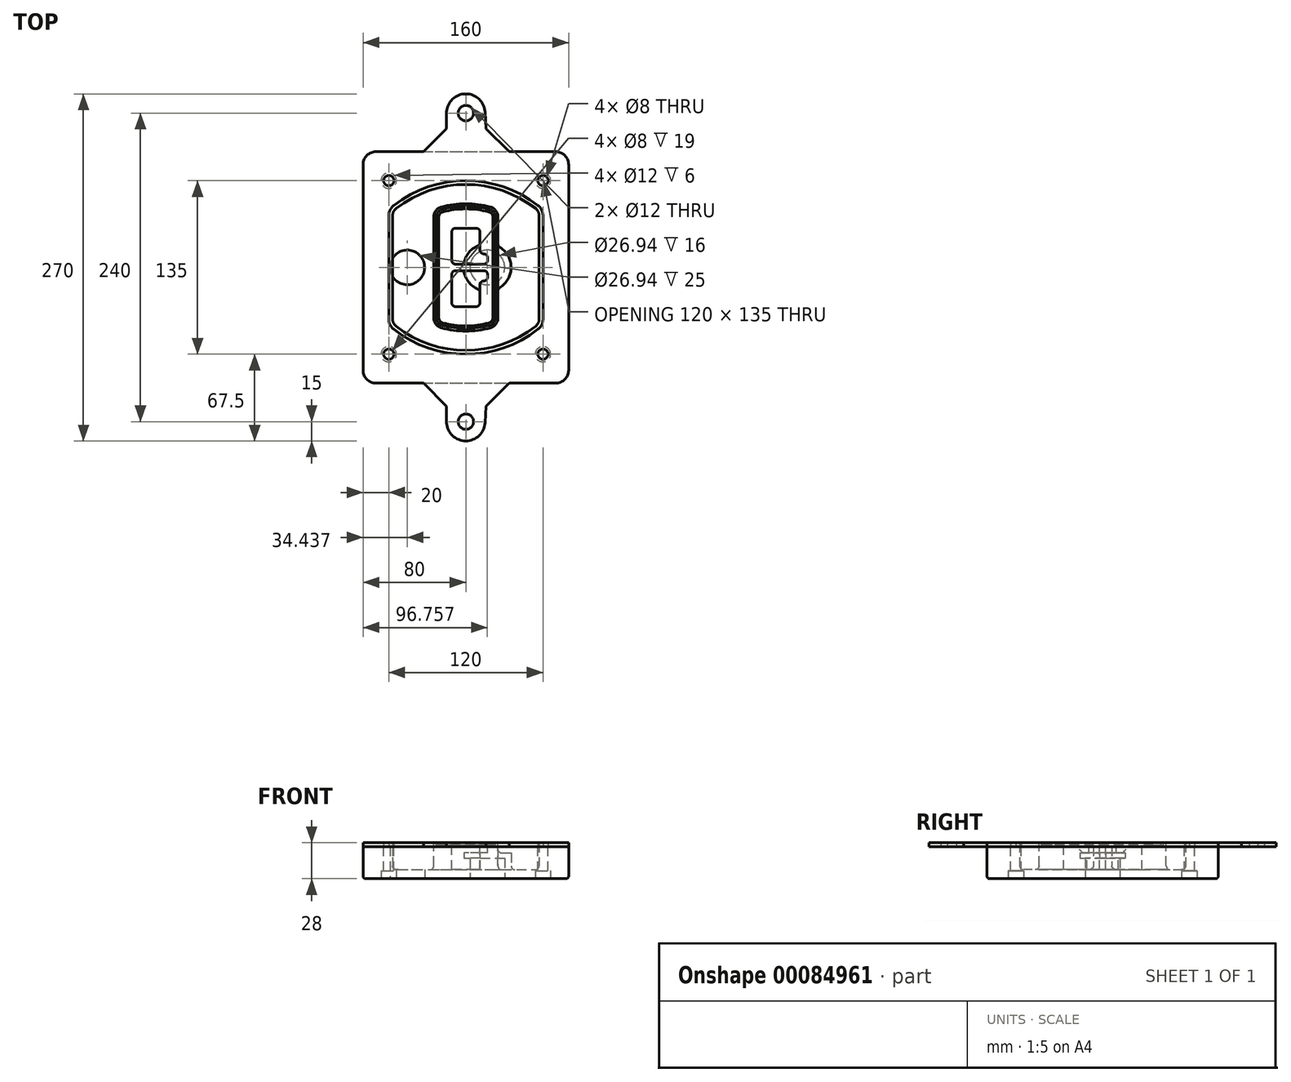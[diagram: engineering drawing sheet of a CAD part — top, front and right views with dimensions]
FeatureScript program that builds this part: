
annotation { "Feature Type Name" : "Feature", "Feature Type Description" : "" }
export const myFeature = defineFeature(function(context is Context, id is Id, definition is map)
    precondition{}
    {
        {
            var Q0;
            Q0=qCreatedBy(makeId("Top.planeOp"),FACE);
            var sketch = newSketch(context, id + "F0", { "sketchPlane" : qUnion([Q0])});
            skPoint(sketch, "E0.rect.middle", {"position": v(0, 0) * mm});
            skLineSegment(sketch, "E1.bottom", {"start": v(-70, -90) * mm, "end": v(70, -90) * mm});
            skLineSegment(sketch, "E1.top", {"start": v(-70, 90) * mm, "end": v(70, 90) * mm});
            skLineSegment(sketch, "E1.left", {"start": v(-80, -80) * mm, "end": v(-80, 80) * mm});
            skLineSegment(sketch, "E1.right", {"start": v(80, -80) * mm, "end": v(80, 80) * mm});
            skLineSegment(sketch, "E2", {"start": v(-80, 90) * mm, "end": v(80, -90) * mm, "construction": true});
            skLineSegment(sketch, "E3", {"start": v(80, 90) * mm, "end": v(-80, -90) * mm, "construction": true});
            skCircle(sketch, "E4", {"center": v(-60, 67.5) * mm, "radius": 4 * mm});
            skCircle(sketch, "E5", {"center": v(60, 67.5) * mm, "radius": 4 * mm});
            skCircle(sketch, "E6", {"center": v(60, -67.5) * mm, "radius": 4 * mm});
            skCircle(sketch, "E7", {"center": v(-60, -67.5) * mm, "radius": 4 * mm});
            skLineSegment(sketch, "E8", {"start": v(-60, 67.5) * mm, "end": v(60, 67.5) * mm, "construction": true});
            skLineSegment(sketch, "E9", {"start": v(60, 67.5) * mm, "end": v(60, -67.5) * mm, "construction": true});
            skLineSegment(sketch, "E10", {"start": v(60, -67.5) * mm, "end": v(-60, -67.5) * mm, "construction": true});
            skLineSegment(sketch, "E11", {"start": v(-60, -67.5) * mm, "end": v(-60, 67.5) * mm, "construction": true});
            skLineSegment(sketch, "E12", {"start": v(-60, 40.3) * mm, "end": v(-60, -40.3) * mm});
            skLineSegment(sketch, "E13", {"start": v(60, 40.3) * mm, "end": v(60, -40.3) * mm});
            skArc(sketch, "E14", {"start": v(56.15, 48.18) * mm, "mid": v(0, 67.5) * mm, "end": v(-56.15, 48.18) * mm});
            skArc(sketch, "E15", {"start": v(-56.15, -48.18) * mm, "mid": v(0, -67.5) * mm, "end": v(56.15, -48.18) * mm});
            skLineSegment(sketch, "E16", {"start": v(-60, 0) * mm, "end": v(60, 0) * mm, "construction": true});
            skPoint(sketch, "E17.visualSharp", {"position": v(-60, -45) * mm});
            skArc(sketch, "E17.filletArc", {"start": v(-60, -40.3) * mm, "mid": v(-58.99, -44.68) * mm, "end": v(-56.15, -48.18) * mm});
            skPoint(sketch, "E18.visualSharp", {"position": v(-60, 45) * mm});
            skArc(sketch, "E18.filletArc", {"start": v(-56.15, 48.18) * mm, "mid": v(-58.99, 44.68) * mm, "end": v(-60, 40.3) * mm});
            skPoint(sketch, "E19.visualSharp", {"position": v(60, 45) * mm});
            skArc(sketch, "E19.filletArc", {"start": v(60, 40.3) * mm, "mid": v(58.99, 44.68) * mm, "end": v(56.15, 48.18) * mm});
            skPoint(sketch, "E20.visualSharp", {"position": v(60, -45) * mm});
            skArc(sketch, "E20.filletArc", {"start": v(56.15, -48.18) * mm, "mid": v(58.99, -44.68) * mm, "end": v(60, -40.3) * mm});
            skPoint(sketch, "E21.visualSharp", {"position": v(-80, 90) * mm});
            skArc(sketch, "E21.filletArc", {"start": v(-70, 90) * mm, "mid": v(-77.07, 87.07) * mm, "end": v(-80, 80) * mm});
            skPoint(sketch, "E22.visualSharp", {"position": v(80, 90) * mm});
            skArc(sketch, "E22.filletArc", {"start": v(80, 80) * mm, "mid": v(77.07, 87.07) * mm, "end": v(70, 90) * mm});
            skPoint(sketch, "E23.visualSharp", {"position": v(80, -90) * mm});
            skArc(sketch, "E23.filletArc", {"start": v(70, -90) * mm, "mid": v(77.07, -87.07) * mm, "end": v(80, -80) * mm});
            skPoint(sketch, "E24.visualSharp", {"position": v(-80, -90) * mm});
            skArc(sketch, "E24.filletArc", {"start": v(-80, -80) * mm, "mid": v(-77.07, -87.07) * mm, "end": v(-70, -90) * mm});
            skArc(sketch, "E25.0", {"start": v(57, 40.3) * mm, "mid": v(56.3, 43.36) * mm, "end": v(54.3, 45.81) * mm});
            skLineSegment(sketch, "E25.1", {"start": v(57, 40.3) * mm, "end": v(57, -40.3) * mm});
            skArc(sketch, "E25.2", {"start": v(54.3, -45.81) * mm, "mid": v(56.3, -43.36) * mm, "end": v(57, -40.3) * mm});
            skArc(sketch, "E25.3", {"start": v(-54.3, -45.81) * mm, "mid": v(0, -64.5) * mm, "end": v(54.3, -45.81) * mm});
            skArc(sketch, "E25.4", {"start": v(-57, -40.3) * mm, "mid": v(-56.3, -43.36) * mm, "end": v(-54.3, -45.81) * mm});
            skArc(sketch, "E25.5", {"start": v(54.3, 45.81) * mm, "mid": v(0, 64.5) * mm, "end": v(-54.3, 45.81) * mm});
            skLineSegment(sketch, "E25.6", {"start": v(-57, 40.3) * mm, "end": v(-57, -40.3) * mm});
            skArc(sketch, "E25.7", {"start": v(-54.3, 45.81) * mm, "mid": v(-56.3, 43.36) * mm, "end": v(-57, 40.3) * mm});
            skArc(sketch, "E26.0", {"start": v(-58.62, 51.33) * mm, "mid": v(-62.58, 46.43) * mm, "end": v(-64, 40.3) * mm});
            skArc(sketch, "E26.1", {"start": v(58.62, 51.33) * mm, "mid": v(0, 71.5) * mm, "end": v(-58.62, 51.33) * mm});
            skArc(sketch, "E26.2", {"start": v(64, 40.3) * mm, "mid": v(62.58, 46.43) * mm, "end": v(58.62, 51.33) * mm});
            skLineSegment(sketch, "E26.3", {"start": v(64, 40.3) * mm, "end": v(64, -40.3) * mm});
            skArc(sketch, "E26.4", {"start": v(58.62, -51.33) * mm, "mid": v(62.58, -46.43) * mm, "end": v(64, -40.3) * mm});
            skLineSegment(sketch, "E26.5", {"start": v(-64, 40.3) * mm, "end": v(-64, -40.3) * mm});
            skArc(sketch, "E26.6", {"start": v(-58.62, -51.33) * mm, "mid": v(0, -71.5) * mm, "end": v(58.62, -51.33) * mm});
            skArc(sketch, "E26.7", {"start": v(-64, -40.3) * mm, "mid": v(-62.58, -46.43) * mm, "end": v(-58.62, -51.33) * mm});
            skSolve(sketch);
        }
        {
            var Q0;
            Q0=makeQuery(id+"F0.imprint","IMPRINT",FACE,{"disambiguationData":[TD([[makeQuery(id+"F0.imprint","IMPRINT",EDGE,{"derivedFrom":sQuery(id+"F0.wireOp",EDGE,"E1.bottom")}),1.0]])]});
            var Q1;
            Q1=makeQuery(id+"F0.imprint","IMPRINT",FACE,{"disambiguationData":[TD([[makeQuery(id+"F0.imprint","IMPRINT",EDGE,{"derivedFrom":sQuery(id+"F0.wireOp",EDGE,"E12")}),1.0]])]});
            var Q2;
            Q2=makeQuery(id+"F0.imprint","IMPRINT",FACE,{"disambiguationData":[TD([[makeQuery(id+"F0.imprint","IMPRINT",EDGE,{"derivedFrom":sQuery(id+"F0.wireOp",EDGE,"E25.0")}),1.0]])]});
            var Q3;
            Q3=makeQuery(id+"F0.imprint","IMPRINT",FACE,{"disambiguationData":[TD([[makeQuery(id+"F0.imprint","IMPRINT",EDGE,{"derivedFrom":sQuery(id+"F0.wireOp",EDGE,"E12")}),-1.0]])]});
            extrude(context, id + "F1", {"entities" : qUnion([Q0, Q1, Q2, Q3]), "oppositeDirection" : true, "depth" : 25 * mm});
        }
        {
            var Q0;
            Q0=makeQuery(id+"F0.imprint","IMPRINT",FACE,{"disambiguationData":[TD([[makeQuery(id+"F0.imprint","IMPRINT",EDGE,{"derivedFrom":sQuery(id+"F0.wireOp",EDGE,"E12")}),1.0]])]});
            extrude(context, id + "F2", {"entities" : qUnion([Q0]), "operationType" : NewBodyOperationType.ADD, "depth" : 3 * mm});
        }
        {
            var Q0;
            Q0=makeQuery(id+"F0.imprint","IMPRINT",FACE,{"disambiguationData":[TD([[makeQuery(id+"F0.imprint","IMPRINT",EDGE,{"derivedFrom":sQuery(id+"F0.wireOp",EDGE,"E25.0")}),1.0]])]});
            extrude(context, id + "F3", {"entities" : qUnion([Q0]), "operationType" : NewBodyOperationType.REMOVE, "oppositeDirection" : true, "depth" : 18 * mm});
        }
        {
            var Q0;
            Q0=makeQuery(id+"F2.opExtrude","CAP_FACE",FACE,{"disambiguationData":[OSD([sQuery(id+"F0.wireOp",EDGE,"E12"),sQuery(id+"F0.wireOp",EDGE,"E13"),sQuery(id+"F0.wireOp",EDGE,"E14"),sQuery(id+"F0.wireOp",EDGE,"E15"),sQuery(id+"F0.wireOp",EDGE,"E17.filletArc"),sQuery(id+"F0.wireOp",EDGE,"E18.filletArc"),sQuery(id+"F0.wireOp",EDGE,"E19.filletArc"),sQuery(id+"F0.wireOp",EDGE,"E20.filletArc"),sQuery(id+"F0.wireOp",EDGE,"E25.0"),sQuery(id+"F0.wireOp",EDGE,"E25.1"),sQuery(id+"F0.wireOp",EDGE,"E25.2"),sQuery(id+"F0.wireOp",EDGE,"E25.3"),sQuery(id+"F0.wireOp",EDGE,"E25.4"),sQuery(id+"F0.wireOp",EDGE,"E25.5"),sQuery(id+"F0.wireOp",EDGE,"E25.6"),sQuery(id+"F0.wireOp",EDGE,"E25.7")])],"isStart":false});
            var sketch = newSketch(context, id + "F4", { "sketchPlane" : qUnion([Q0])});
            skArc(sketch, "E27.0", {"start": v(-19.08, -46.97) * mm, "mid": v(0, -49.5) * mm, "end": v(19.08, -46.97) * mm});
            skArc(sketch, "E28.0", {"start": v(19.08, 46.97) * mm, "mid": v(0, 49.5) * mm, "end": v(-19.08, 46.97) * mm});
            skLineSegment(sketch, "E29", {"start": v(-25, 39.25) * mm, "end": v(-25, -39.25) * mm});
            skLineSegment(sketch, "E30", {"start": v(25, 39.25) * mm, "end": v(25, -39.25) * mm});
            skLineSegment(sketch, "E31", {"start": v(-25, 45.1) * mm, "end": v(25, 45.1) * mm, "construction": true});
            skLineSegment(sketch, "E32", {"start": v(-25, -45.1) * mm, "end": v(25, -45.1) * mm, "construction": true});
            skPoint(sketch, "E33.visualSharp", {"position": v(-25, 45.1) * mm});
            skArc(sketch, "E33.filletArc", {"start": v(-19.08, 46.97) * mm, "mid": v(-23.35, 44.11) * mm, "end": v(-25, 39.25) * mm});
            skPoint(sketch, "E34.visualSharp", {"position": v(25, 45.1) * mm});
            skArc(sketch, "E34.filletArc", {"start": v(25, 39.25) * mm, "mid": v(23.35, 44.11) * mm, "end": v(19.08, 46.97) * mm});
            skPoint(sketch, "E35.visualSharp", {"position": v(25, -45.1) * mm});
            skArc(sketch, "E35.filletArc", {"start": v(19.08, -46.97) * mm, "mid": v(23.35, -44.11) * mm, "end": v(25, -39.25) * mm});
            skPoint(sketch, "E36.visualSharp", {"position": v(-25, -45.1) * mm});
            skArc(sketch, "E36.filletArc", {"start": v(-25, -39.25) * mm, "mid": v(-23.35, -44.11) * mm, "end": v(-19.08, -46.97) * mm});
            skArc(sketch, "E37.0", {"start": v(54.3, 45.81) * mm, "mid": v(0, 64.5) * mm, "end": v(-54.3, 45.81) * mm});
            skArc(sketch, "E37.1", {"start": v(-54.3, 45.81) * mm, "mid": v(-56.3, 43.36) * mm, "end": v(-57, 40.3) * mm});
            skLineSegment(sketch, "E37.2", {"start": v(-57, 40.3) * mm, "end": v(-57, -40.3) * mm});
            skArc(sketch, "E37.3", {"start": v(-57, -40.3) * mm, "mid": v(-56.3, -43.36) * mm, "end": v(-54.3, -45.81) * mm});
            skArc(sketch, "E37.4", {"start": v(-54.3, -45.81) * mm, "mid": v(0, -64.5) * mm, "end": v(54.3, -45.81) * mm});
            skArc(sketch, "E37.5", {"start": v(54.3, -45.81) * mm, "mid": v(56.3, -43.36) * mm, "end": v(57, -40.3) * mm});
            skLineSegment(sketch, "E37.6", {"start": v(57, 40.3) * mm, "end": v(57, -40.3) * mm});
            skArc(sketch, "E37.7", {"start": v(57, 40.3) * mm, "mid": v(56.3, 43.36) * mm, "end": v(54.3, 45.81) * mm});
            skLineSegment(sketch, "E38.0", {"start": v(23, 39.25) * mm, "end": v(23, -39.25) * mm});
            skArc(sketch, "E38.1", {"start": v(18.56, -45.04) * mm, "mid": v(21.76, -42.9) * mm, "end": v(23, -39.25) * mm});
            skArc(sketch, "E38.2", {"start": v(-18.56, -45.04) * mm, "mid": v(0, -47.5) * mm, "end": v(18.56, -45.04) * mm});
            skArc(sketch, "E38.3", {"start": v(-23, -39.25) * mm, "mid": v(-21.76, -42.9) * mm, "end": v(-18.56, -45.04) * mm});
            skLineSegment(sketch, "E38.4", {"start": v(-23, 39.25) * mm, "end": v(-23, -39.25) * mm});
            skArc(sketch, "E38.5", {"start": v(23, 39.25) * mm, "mid": v(21.76, 42.9) * mm, "end": v(18.56, 45.04) * mm});
            skArc(sketch, "E38.6", {"start": v(-18.56, 45.04) * mm, "mid": v(-21.76, 42.9) * mm, "end": v(-23, 39.25) * mm});
            skArc(sketch, "E38.7", {"start": v(18.56, 45.04) * mm, "mid": v(0, 47.5) * mm, "end": v(-18.56, 45.04) * mm});
            skArc(sketch, "E39.0", {"start": v(21, 39.25) * mm, "mid": v(20.18, 41.68) * mm, "end": v(18.04, 43.1) * mm});
            skLineSegment(sketch, "E39.1", {"start": v(21, 39.25) * mm, "end": v(21, -39.25) * mm});
            skArc(sketch, "E39.2", {"start": v(18.04, -43.1) * mm, "mid": v(20.18, -41.68) * mm, "end": v(21, -39.25) * mm});
            skArc(sketch, "E39.3", {"start": v(-18.04, -43.1) * mm, "mid": v(0, -45.5) * mm, "end": v(18.04, -43.1) * mm});
            skArc(sketch, "E39.4", {"start": v(-21, -39.25) * mm, "mid": v(-20.18, -41.68) * mm, "end": v(-18.04, -43.1) * mm});
            skArc(sketch, "E39.5", {"start": v(18.04, 43.1) * mm, "mid": v(0, 45.5) * mm, "end": v(-18.04, 43.1) * mm});
            skLineSegment(sketch, "E39.6", {"start": v(-21, 39.25) * mm, "end": v(-21, -39.25) * mm});
            skArc(sketch, "E39.7", {"start": v(-18.04, 43.1) * mm, "mid": v(-20.18, 41.68) * mm, "end": v(-21, 39.25) * mm});
            skLineSegment(sketch, "E40", {"start": v(-25, 0) * mm, "end": v(25, 0) * mm, "construction": true});
            skLineSegment(sketch, "E41", {"start": v(-11, 5.5) * mm, "end": v(-11, 27.5) * mm});
            skLineSegment(sketch, "E42", {"start": v(-8, 30.5) * mm, "end": v(8, 30.5) * mm});
            skLineSegment(sketch, "E43", {"start": v(11, 27.5) * mm, "end": v(11, 13.5) * mm});
            skLineSegment(sketch, "E44", {"start": v(14, 10.5) * mm, "end": v(14, 10.5) * mm});
            skLineSegment(sketch, "E45", {"start": v(17, 7.5) * mm, "end": v(17, 5.5) * mm});
            skLineSegment(sketch, "E46", {"start": v(14, 2.5) * mm, "end": v(-8, 2.5) * mm});
            skPoint(sketch, "E47.visualSharp", {"position": v(-11, 30.5) * mm});
            skArc(sketch, "E47.filletArc", {"start": v(-8, 30.5) * mm, "mid": v(-10.12, 29.62) * mm, "end": v(-11, 27.5) * mm});
            skPoint(sketch, "E48.visualSharp", {"position": v(11, 30.5) * mm});
            skArc(sketch, "E48.filletArc", {"start": v(11, 27.5) * mm, "mid": v(10.12, 29.62) * mm, "end": v(8, 30.5) * mm});
            skPoint(sketch, "E49.visualSharp", {"position": v(11, 10.5) * mm});
            skArc(sketch, "E49.filletArc", {"start": v(11, 13.5) * mm, "mid": v(11.88, 11.38) * mm, "end": v(14, 10.5) * mm});
            skPoint(sketch, "E50.visualSharp", {"position": v(17, 10.5) * mm});
            skArc(sketch, "E50.filletArc", {"start": v(17, 7.5) * mm, "mid": v(16.12, 9.62) * mm, "end": v(14, 10.5) * mm});
            skPoint(sketch, "E51.visualSharp", {"position": v(17, 2.5) * mm});
            skArc(sketch, "E51.filletArc", {"start": v(14, 2.5) * mm, "mid": v(16.12, 3.38) * mm, "end": v(17, 5.5) * mm});
            skPoint(sketch, "E52.visualSharp", {"position": v(-11, 2.5) * mm});
            skArc(sketch, "E52.filletArc", {"start": v(-11, 5.5) * mm, "mid": v(-10.12, 3.38) * mm, "end": v(-8, 2.5) * mm});
            skLineSegment(sketch, "E53.0.MirrorCS", {"start": v(14, -2.5) * mm, "end": v(-8, -2.5) * mm});
            skArc(sketch, "E54.0.MirrorCS", {"start": v(-11, -5.5) * mm, "mid": v(-10.12, -3.38) * mm, "end": v(-8, -2.5) * mm});
            skLineSegment(sketch, "E55.0.MirrorCS", {"start": v(-11, -5.5) * mm, "end": v(-11, -27.5) * mm});
            skArc(sketch, "E56.0.MirrorCS", {"start": v(-8, -30.5) * mm, "mid": v(-10.12, -29.62) * mm, "end": v(-11, -27.5) * mm});
            skLineSegment(sketch, "E57.0.MirrorCS", {"start": v(-8, -30.5) * mm, "end": v(8, -30.5) * mm});
            skArc(sketch, "E58.0.MirrorCS", {"start": v(11, -27.5) * mm, "mid": v(10.12, -29.62) * mm, "end": v(8, -30.5) * mm});
            skLineSegment(sketch, "E59.0.MirrorCS", {"start": v(11, -27.5) * mm, "end": v(11, -13.5) * mm});
            skArc(sketch, "E60.0.MirrorCS", {"start": v(11, -13.5) * mm, "mid": v(11.88, -11.38) * mm, "end": v(14, -10.5) * mm});
            skArc(sketch, "E61.0.MirrorCS", {"start": v(17, -7.5) * mm, "mid": v(16.12, -9.62) * mm, "end": v(14, -10.5) * mm});
            skLineSegment(sketch, "E62.0.MirrorCS", {"start": v(17, -7.5) * mm, "end": v(17, -5.5) * mm});
            skArc(sketch, "E63.0.MirrorCS", {"start": v(14, -2.5) * mm, "mid": v(16.12, -3.38) * mm, "end": v(17, -5.5) * mm});
            skSolve(sketch);
        }
        {
            var Q0;
            Q0=makeQuery(id+"F4.imprint","IMPRINT",FACE,{"disambiguationData":[TD([[makeQuery(id+"F4.imprint","IMPRINT",EDGE,{"derivedFrom":sQuery(id+"F4.wireOp",EDGE,"E27.0")}),1.0]])]});
            var Q1;
            Q1=makeQuery(id+"F4.imprint","IMPRINT",FACE,{"disambiguationData":[TD([[makeQuery(id+"F4.imprint","IMPRINT",EDGE,{"derivedFrom":sQuery(id+"F4.wireOp",EDGE,"E38.0")}),-1.0]])]});
            var Q2;
            Q2=makeQuery(id+"F4.imprint","IMPRINT",FACE,{"disambiguationData":[TD([[makeQuery(id+"F4.imprint","IMPRINT",EDGE,{"derivedFrom":sQuery(id+"F4.wireOp",EDGE,"E39.0")}),1.0]])]});
            extrude(context, id + "F5", {"entities" : qUnion([Q0, Q1, Q2]), "operationType" : NewBodyOperationType.ADD, "endBound" : BoundingType.UP_TO_NEXT, "oppositeDirection" : true, "depth" : 25 * mm});
        }
        {
            var Q0;
            Q0=makeQuery(id+"F4.imprint","IMPRINT",FACE,{"disambiguationData":[TD([[makeQuery(id+"F4.imprint","IMPRINT",EDGE,{"derivedFrom":sQuery(id+"F4.wireOp",EDGE,"E38.0")}),-1.0]])]});
            extrude(context, id + "F6", {"entities" : qUnion([Q0]), "operationType" : NewBodyOperationType.REMOVE, "oppositeDirection" : true, "depth" : 2 * mm});
        }
        {
            var Q0;
            Q0=makeQuery(id+"F1.opExtrude","CAP_FACE",FACE,{"disambiguationData":[OSD([sQuery(id+"F0.wireOp",EDGE,"E1.bottom"),sQuery(id+"F0.wireOp",EDGE,"E1.top"),sQuery(id+"F0.wireOp",EDGE,"E1.left"),sQuery(id+"F0.wireOp",EDGE,"E1.right"),sQuery(id+"F0.wireOp",EDGE,"E4"),sQuery(id+"F0.wireOp",EDGE,"E5"),sQuery(id+"F0.wireOp",EDGE,"E6"),sQuery(id+"F0.wireOp",EDGE,"E7"),sQuery(id+"F0.wireOp",EDGE,"E21.filletArc"),sQuery(id+"F0.wireOp",EDGE,"E22.filletArc"),sQuery(id+"F0.wireOp",EDGE,"E23.filletArc"),sQuery(id+"F0.wireOp",EDGE,"E24.filletArc")])],"isStart":false});
            var sketch = newSketch(context, id + "F7", { "sketchPlane" : qUnion([Q0])});
            skCircle(sketch, "E64", {"center": v(16.76, 0) * mm, "radius": 13.47 * mm});
            skCircle(sketch, "E65", {"center": v(-45.56, 0) * mm, "radius": 13.47 * mm});
            skLineSegment(sketch, "E66", {"start": v(80, 0) * mm, "end": v(-80, 0) * mm});
            skCircle(sketch, "E67", {"center": v(16.76, 0) * mm, "radius": 18.47 * mm});
            skCircle(sketch, "E68", {"center": v(60, -67.5) * mm, "radius": 6 * mm});
            skCircle(sketch, "E69", {"center": v(-60, -67.5) * mm, "radius": 6 * mm});
            skCircle(sketch, "E70", {"center": v(-60, 67.5) * mm, "radius": 6 * mm});
            skCircle(sketch, "E71", {"center": v(60, 67.5) * mm, "radius": 6 * mm});
            skSolve(sketch);
        }
        {
            var Q0;
            {var subQ1=sQuery(id+"F7.wireOp",EDGE,"E66");var subQ4=sQuery(id+"F7.wireOp",EDGE,"E64");var subQ6=makeQuery(id+"F7.imprint","INTERSECT",VERTEX,{"disambiguationData":[OD(0.0)],"derivedFrom":[subQ4,subQ1]});Q0=makeQuery(id+"F7.imprint","IMPRINT",FACE,{"disambiguationData":[TD([[makeQuery(id+"F7.imprint","IMPRINT",EDGE,{"disambiguationData":[TD([[subQ6,-1.0]])],"derivedFrom":subQ4}),-1.0]])]});}
            var Q1;
            {var subQ0=sQuery(id+"F7.wireOp",EDGE,"E66");var subQ1=sQuery(id+"F7.wireOp",EDGE,"E64");var subQ3=makeQuery(id+"F7.imprint","INTERSECT",VERTEX,{"disambiguationData":[OD(0.0)],"derivedFrom":[subQ1,subQ0]});Q1=makeQuery(id+"F7.imprint","IMPRINT",FACE,{"disambiguationData":[TD([[makeQuery(id+"F7.imprint","IMPRINT",EDGE,{"disambiguationData":[TD([[subQ3,-1.0]])],"derivedFrom":subQ1}),1.0]])]});}
            var Q2;
            {var subQ0=sQuery(id+"F7.wireOp",EDGE,"E66");var subQ1=sQuery(id+"F7.wireOp",EDGE,"E64");var subQ3=makeQuery(id+"F7.imprint","INTERSECT",VERTEX,{"disambiguationData":[OD(0.0)],"derivedFrom":[subQ1,subQ0]});Q2=makeQuery(id+"F7.imprint","IMPRINT",FACE,{"disambiguationData":[TD([[makeQuery(id+"F7.imprint","IMPRINT",EDGE,{"disambiguationData":[TD([[subQ3,1.0]])],"derivedFrom":subQ1}),1.0]])]});}
            var Q3;
            {var subQ1=sQuery(id+"F7.wireOp",EDGE,"E66");var subQ4=sQuery(id+"F7.wireOp",EDGE,"E64");var subQ6=makeQuery(id+"F7.imprint","INTERSECT",VERTEX,{"disambiguationData":[OD(0.0)],"derivedFrom":[subQ4,subQ1]});Q3=makeQuery(id+"F7.imprint","IMPRINT",FACE,{"disambiguationData":[TD([[makeQuery(id+"F7.imprint","IMPRINT",EDGE,{"disambiguationData":[TD([[subQ6,1.0]])],"derivedFrom":subQ4}),-1.0]])]});}
            extrude(context, id + "F8", {"entities" : qUnion([Q0, Q1, Q2, Q3]), "operationType" : NewBodyOperationType.ADD, "oppositeDirection" : true, "depth" : 20 * mm});
        }
        {
            var Q0;
            {var subQ0=sQuery(id+"F7.wireOp",EDGE,"E66");var subQ1=sQuery(id+"F7.wireOp",EDGE,"E64");var subQ3=makeQuery(id+"F7.imprint","INTERSECT",VERTEX,{"disambiguationData":[OD(0.0)],"derivedFrom":[subQ1,subQ0]});Q0=makeQuery(id+"F7.imprint","IMPRINT",FACE,{"disambiguationData":[TD([[makeQuery(id+"F7.imprint","IMPRINT",EDGE,{"disambiguationData":[TD([[subQ3,-1.0]])],"derivedFrom":subQ1}),1.0]])]});}
            var Q1;
            {var subQ0=sQuery(id+"F7.wireOp",EDGE,"E66");var subQ1=sQuery(id+"F7.wireOp",EDGE,"E64");var subQ3=makeQuery(id+"F7.imprint","INTERSECT",VERTEX,{"disambiguationData":[OD(0.0)],"derivedFrom":[subQ1,subQ0]});Q1=makeQuery(id+"F7.imprint","IMPRINT",FACE,{"disambiguationData":[TD([[makeQuery(id+"F7.imprint","IMPRINT",EDGE,{"disambiguationData":[TD([[subQ3,1.0]])],"derivedFrom":subQ1}),1.0]])]});}
            extrude(context, id + "F9", {"entities" : qUnion([Q0, Q1]), "operationType" : NewBodyOperationType.REMOVE, "oppositeDirection" : true, "depth" : 16 * mm});
        }
        {
            var Q0;
            {var subQ0=sQuery(id+"F7.wireOp",EDGE,"E66");var subQ1=sQuery(id+"F7.wireOp",EDGE,"E65");var subQ3=makeQuery(id+"F7.imprint","INTERSECT",VERTEX,{"disambiguationData":[OD(0.0)],"derivedFrom":[subQ1,subQ0]});Q0=makeQuery(id+"F7.imprint","IMPRINT",FACE,{"disambiguationData":[TD([[makeQuery(id+"F7.imprint","IMPRINT",EDGE,{"disambiguationData":[TD([[subQ3,-1.0]])],"derivedFrom":subQ1}),1.0]])]});}
            var Q1;
            {var subQ0=sQuery(id+"F7.wireOp",EDGE,"E66");var subQ1=sQuery(id+"F7.wireOp",EDGE,"E65");var subQ3=makeQuery(id+"F7.imprint","INTERSECT",VERTEX,{"disambiguationData":[OD(0.0)],"derivedFrom":[subQ1,subQ0]});Q1=makeQuery(id+"F7.imprint","IMPRINT",FACE,{"disambiguationData":[TD([[makeQuery(id+"F7.imprint","IMPRINT",EDGE,{"disambiguationData":[TD([[subQ3,1.0]])],"derivedFrom":subQ1}),1.0]])]});}
            extrude(context, id + "F10", {"entities" : qUnion([Q0, Q1]), "operationType" : NewBodyOperationType.REMOVE, "oppositeDirection" : true, "depth" : 25 * mm});
        }
        {
            var Q0;
            Q0=makeQuery(id+"F7.imprint","IMPRINT",FACE,{"disambiguationData":[TD([[makeQuery(id+"F7.imprint","IMPRINT",EDGE,{"derivedFrom":sQuery(id+"F7.wireOp",EDGE,"E68")}),1.0]])]});
            var Q1;
            Q1=makeQuery(id+"F7.imprint","IMPRINT",FACE,{"disambiguationData":[TD([[makeQuery(id+"F7.imprint","IMPRINT",EDGE,{"derivedFrom":makeQuery(id+"F1.opExtrude","CAP_EDGE",EDGE,{"disambiguationData":[OSD([sQuery(id+"F0.wireOp",EDGE,"E5")])],"isStart":false})}),-1.0]])]});
            var Q2;
            Q2=makeQuery(id+"F7.imprint","IMPRINT",FACE,{"disambiguationData":[TD([[makeQuery(id+"F7.imprint","IMPRINT",EDGE,{"derivedFrom":sQuery(id+"F7.wireOp",EDGE,"E69")}),1.0]])]});
            var Q3;
            Q3=makeQuery(id+"F7.imprint","IMPRINT",FACE,{"disambiguationData":[TD([[makeQuery(id+"F7.imprint","IMPRINT",EDGE,{"derivedFrom":makeQuery(id+"F1.opExtrude","CAP_EDGE",EDGE,{"disambiguationData":[OSD([sQuery(id+"F0.wireOp",EDGE,"E4")])],"isStart":false})}),-1.0]])]});
            var Q4;
            Q4=makeQuery(id+"F7.imprint","IMPRINT",FACE,{"disambiguationData":[TD([[makeQuery(id+"F7.imprint","IMPRINT",EDGE,{"derivedFrom":sQuery(id+"F7.wireOp",EDGE,"E70")}),1.0]])]});
            var Q5;
            Q5=makeQuery(id+"F7.imprint","IMPRINT",FACE,{"disambiguationData":[TD([[makeQuery(id+"F7.imprint","IMPRINT",EDGE,{"derivedFrom":makeQuery(id+"F1.opExtrude","CAP_EDGE",EDGE,{"disambiguationData":[OSD([sQuery(id+"F0.wireOp",EDGE,"E7")])],"isStart":false})}),-1.0]])]});
            var Q6;
            Q6=makeQuery(id+"F7.imprint","IMPRINT",FACE,{"disambiguationData":[TD([[makeQuery(id+"F7.imprint","IMPRINT",EDGE,{"derivedFrom":sQuery(id+"F7.wireOp",EDGE,"E71")}),1.0]])]});
            var Q7;
            Q7=makeQuery(id+"F7.imprint","IMPRINT",FACE,{"disambiguationData":[TD([[makeQuery(id+"F7.imprint","IMPRINT",EDGE,{"derivedFrom":makeQuery(id+"F1.opExtrude","CAP_EDGE",EDGE,{"disambiguationData":[OSD([sQuery(id+"F0.wireOp",EDGE,"E6")])],"isStart":false})}),-1.0]])]});
            extrude(context, id + "F11", {"entities" : qUnion([Q0, Q1, Q2, Q3, Q4, Q5, Q6, Q7]), "operationType" : NewBodyOperationType.REMOVE, "oppositeDirection" : true, "depth" : 6 * mm});
        }
        {
            var Q0;
            Q0=makeQuery(id+"F9.boolean.opBoolean","COPY",FACE,{"derivedFrom":makeQuery(id+"F9.opExtrude","CAP_FACE",FACE,{"disambiguationData":[OSD([sQuery(id+"F7.wireOp",EDGE,"E64")])],"isStart":false})});
            var sketch = newSketch(context, id + "F12", { "sketchPlane" : qUnion([Q0])});
            skArc(sketch, "E72.0", {"start": v(11, 17.55) * mm, "mid": v(2.57, 11.82) * mm, "end": v(-1.54, 2.5) * mm});
            skArc(sketch, "E72.1", {"start": v(-1.54, -2.5) * mm, "mid": v(2.57, -11.82) * mm, "end": v(11, -17.55) * mm});
            skLineSegment(sketch, "E73", {"start": v(-1.54, -2.5) * mm, "end": v(14, -2.5) * mm});
            skLineSegment(sketch, "E74.0", {"start": v(14, 2.5) * mm, "end": v(-1.54, 2.5) * mm});
            skArc(sketch, "E74.1", {"start": v(14, 2.5) * mm, "mid": v(16.12, 3.38) * mm, "end": v(17, 5.5) * mm});
            skLineSegment(sketch, "E74.2", {"start": v(17, 7.5) * mm, "end": v(17, 5.5) * mm});
            skArc(sketch, "E74.3", {"start": v(17, 7.5) * mm, "mid": v(16.12, 9.62) * mm, "end": v(14, 10.5) * mm});
            skArc(sketch, "E74.4", {"start": v(11, 13.5) * mm, "mid": v(11.88, 11.38) * mm, "end": v(14, 10.5) * mm});
            skLineSegment(sketch, "E74.5", {"start": v(11, 17.55) * mm, "end": v(11, 13.5) * mm});
            skLineSegment(sketch, "E74.7", {"start": v(14, -2.5) * mm, "end": v(-1.54, -2.5) * mm});
            skArc(sketch, "E74.8", {"start": v(14, -2.5) * mm, "mid": v(16.12, -3.38) * mm, "end": v(17, -5.5) * mm});
            skLineSegment(sketch, "E74.9", {"start": v(17, -7.5) * mm, "end": v(17, -5.5) * mm});
            skArc(sketch, "E74.10", {"start": v(17, -7.5) * mm, "mid": v(16.12, -9.62) * mm, "end": v(14, -10.5) * mm});
            skArc(sketch, "E74.11", {"start": v(11, -13.5) * mm, "mid": v(11.88, -11.38) * mm, "end": v(14, -10.5) * mm});
            skLineSegment(sketch, "E74.12", {"start": v(11, -17.55) * mm, "end": v(11, -13.5) * mm});
            skPoint(sketch, "E75.orphan", {"position": v(11, -27.5) * mm});
            skPoint(sketch, "E76.orphan", {"position": v(-8, -2.5) * mm});
            skPoint(sketch, "E77.orphan", {"position": v(-8, 2.5) * mm});
            skPoint(sketch, "E78.orphan", {"position": v(11, 27.5) * mm});
            skSolve(sketch);
        }
        {
            var Q0;
            {var subQ7=sQuery(id+"F12.wireOp",EDGE,"E72.0");var subQ14=sQuery(id+"F12.wireOp",EDGE,"E72.1");var subQ16=sQuery(id+"F12.wireOp",EDGE,"E74.1");var subQ18=sQuery(id+"F12.wireOp",EDGE,"E74.8");Q0=qUnion([makeQuery(id+"F12.imprint","IMPRINT",FACE,{"disambiguationData":[TD([[makeQuery(id+"F12.imprint","IMPRINT",EDGE,{"derivedFrom":subQ7}),1.0]])]}),makeQuery(id+"F12.imprint","IMPRINT",FACE,{"disambiguationData":[TD([[makeQuery(id+"F12.imprint","IMPRINT",EDGE,{"derivedFrom":subQ14}),1.0]])]}),makeQuery(id+"F12.imprint","IMPRINT",FACE,{"disambiguationData":[TD([[makeQuery(id+"F12.imprint","IMPRINT",EDGE,{"derivedFrom":subQ16}),1.0]])]}),makeQuery(id+"F12.imprint","IMPRINT",FACE,{"disambiguationData":[TD([[makeQuery(id+"F12.imprint","IMPRINT",EDGE,{"derivedFrom":subQ18}),-1.0]])]})]);}
            var Q1;
            Q1=makeQuery(id+"F5.boolean.opBoolean","SPLIT",FACE,{"disambiguationData":[TD([makeQuery(id+"F5.opExtrude","SWEPT_FACE",FACE,{"disambiguationData":[OSD([sQuery(id+"F4.wireOp",EDGE,"E41")])]})])],"derivedFrom":makeQuery(id+"F3.boolean.opBoolean","COPY",FACE,{"derivedFrom":makeQuery(id+"F3.opExtrude","CAP_FACE",FACE,{"disambiguationData":[OSD([sQuery(id+"F0.wireOp",EDGE,"E25.0"),sQuery(id+"F0.wireOp",EDGE,"E25.1"),sQuery(id+"F0.wireOp",EDGE,"E25.2"),sQuery(id+"F0.wireOp",EDGE,"E25.3"),sQuery(id+"F0.wireOp",EDGE,"E25.4"),sQuery(id+"F0.wireOp",EDGE,"E25.5"),sQuery(id+"F0.wireOp",EDGE,"E25.6"),sQuery(id+"F0.wireOp",EDGE,"E25.7")])],"isStart":false})})});
            extrude(context, id + "F13", {"entities" : qUnion([Q0]), "operationType" : NewBodyOperationType.REMOVE, "endBound" : BoundingType.UP_TO_SURFACE, "endBoundEntityFace" : qUnion([Q1]), "depth" : 25 * mm});
        }
        {
            var Q0;
            Q0=makeQuery(id+"F3.boolean.opBoolean","COPY",EDGE,{"derivedFrom":makeQuery(id+"F3.opExtrude","CAP_EDGE",EDGE,{"disambiguationData":[OSD([sQuery(id+"F0.wireOp",EDGE,"E25.6")])],"isStart":false})});
            var Q1;
            Q1=makeQuery(id+"F8.boolean.opBoolean","INTERSECT",EDGE,{"derivedFrom":[makeQuery(id+"F5.opExtrude","SWEPT_FACE",FACE,{"disambiguationData":[OSD([sQuery(id+"F4.wireOp",EDGE,"E30")])]}),makeQuery(id+"F8.opExtrude","CAP_FACE",FACE,{"disambiguationData":[OSD([sQuery(id+"F7.wireOp",EDGE,"E67")])],"isStart":false})]});
            var Q2;
            Q2=makeQuery(id+"F8.boolean.opBoolean","INTERSECT",EDGE,{"disambiguationData":[OD(1.0)],"derivedFrom":[makeQuery(id+"F5.opExtrude","SWEPT_FACE",FACE,{"disambiguationData":[OSD([sQuery(id+"F4.wireOp",EDGE,"E30")])]}),makeQuery(id+"F8.opExtrude","SWEPT_FACE",FACE,{"disambiguationData":[OSD([sQuery(id+"F7.wireOp",EDGE,"E67")])]})]});
            var Q3;
            {var subQ0=sQuery(id+"F4.wireOp",EDGE,"E30");Q3=makeQuery(id+"F8.boolean.opBoolean","SPLIT",EDGE,{"disambiguationData":[TD([makeQuery(id+"F5.opExtrude","SWEPT_FACE",FACE,{"disambiguationData":[OSD([sQuery(id+"F4.wireOp",EDGE,"E35.filletArc")])]})])],"derivedFrom":makeQuery(id+"F5.opExtrude","CAP_EDGE",EDGE,{"disambiguationData":[OSD([subQ0])],"isStart":false})});}
            var Q4;
            {var subQ0=sQuery(id+"F0.wireOp",EDGE,"E25.7");var subQ1=sQuery(id+"F0.wireOp",EDGE,"E25.1");var subQ2=sQuery(id+"F0.wireOp",EDGE,"E25.6");var subQ3=sQuery(id+"F0.wireOp",EDGE,"E25.5");var subQ4=sQuery(id+"F0.wireOp",EDGE,"E25.4");var subQ5=sQuery(id+"F0.wireOp",EDGE,"E25.0");var subQ6=sQuery(id+"F0.wireOp",EDGE,"E25.2");var subQ7=sQuery(id+"F0.wireOp",EDGE,"E25.3");Q4=makeQuery(id+"F8.boolean.opBoolean","INTERSECT",EDGE,{"derivedFrom":[makeQuery(id+"F5.boolean.opBoolean","SPLIT",FACE,{"disambiguationData":[TD([makeQuery(id+"F2.opExtrude","SWEPT_FACE",FACE,{"disambiguationData":[OSD([subQ5])]})])],"derivedFrom":makeQuery(id+"F3.boolean.opBoolean","COPY",FACE,{"derivedFrom":makeQuery(id+"F3.opExtrude","CAP_FACE",FACE,{"disambiguationData":[OSD([subQ5,subQ1,subQ6,subQ7,subQ4,subQ3,subQ2,subQ0])],"isStart":false})})}),makeQuery(id+"F8.opExtrude","SWEPT_FACE",FACE,{"disambiguationData":[OSD([sQuery(id+"F7.wireOp",EDGE,"E67")])]})]});}
            var Q5;
            Q5=makeQuery(id+"F8.boolean.opBoolean","INTERSECT",EDGE,{"disambiguationData":[OD(0.0)],"derivedFrom":[makeQuery(id+"F5.opExtrude","SWEPT_FACE",FACE,{"disambiguationData":[OSD([sQuery(id+"F4.wireOp",EDGE,"E30")])]}),makeQuery(id+"F8.opExtrude","SWEPT_FACE",FACE,{"disambiguationData":[OSD([sQuery(id+"F7.wireOp",EDGE,"E67")])]})]});
            fillet(context, id + "F14", {"entities" : qUnion([Q0, Q1, Q2, Q3, Q4, Q5]), "radius" : 3 * mm, "tangentPropagation" : true, "allowEdgeOverflow" : false});
        }
        {
            var Q0;
            Q0=makeQuery(id+"F1.opExtrude","CAP_EDGE",EDGE,{"disambiguationData":[OSD([sQuery(id+"F0.wireOp",EDGE,"E1.bottom")])],"isStart":false});
            fillet(context, id + "F15", {"entities" : qUnion([Q0]), "radius" : 2 * mm, "tangentPropagation" : true, "allowEdgeOverflow" : false});
        }
        {
            var Q0;
            {var subQ0=sQuery(id+"F0.wireOp",EDGE,"E22.filletArc");var subQ1=sQuery(id+"F0.wireOp",EDGE,"E7");var subQ2=sQuery(id+"F0.wireOp",EDGE,"E6");var subQ3=sQuery(id+"F0.wireOp",EDGE,"E5");var subQ4=sQuery(id+"F0.wireOp",EDGE,"E4");var subQ5=sQuery(id+"F0.wireOp",EDGE,"E1.bottom");var subQ6=sQuery(id+"F0.wireOp",EDGE,"E21.filletArc");var subQ7=sQuery(id+"F0.wireOp",EDGE,"E1.top");var subQ8=sQuery(id+"F0.wireOp",EDGE,"E1.left");var subQ9=sQuery(id+"F0.wireOp",EDGE,"E1.right");var subQ10=sQuery(id+"F0.wireOp",EDGE,"E23.filletArc");var subQ11=sQuery(id+"F0.wireOp",EDGE,"E24.filletArc");Q0=makeQuery(id+"F2.boolean.opBoolean","SPLIT",FACE,{"disambiguationData":[TD([makeQuery(id+"F1.opExtrude","SWEPT_FACE",FACE,{"disambiguationData":[OSD([subQ5])]})])],"derivedFrom":makeQuery(id+"F1.opExtrude","CAP_FACE",FACE,{"disambiguationData":[OSD([subQ5,subQ7,subQ8,subQ9,subQ4,subQ3,subQ2,subQ1,subQ6,subQ0,subQ10,subQ11])],"isStart":true})});}
            var sketch = newSketch(context, id + "F16", { "sketchPlane" : qUnion([Q0])});
            skCircle(sketch, "E79", {"center": v(0, 120) * mm, "radius": 6 * mm});
            skPoint(sketch, "E79.centerSnap0", {"position": v(0, 90) * mm});
            skArc(sketch, "E80", {"start": v(14.98, 120.83) * mm, "mid": v(0, 135) * mm, "end": v(-14.98, 120.85) * mm});
            skLineSegment(sketch, "E81", {"start": v(-14.98, 120.85) * mm, "end": v(-14.98, 108) * mm});
            skLineSegment(sketch, "E82", {"start": v(14.98, 120.83) * mm, "end": v(15.68, 108) * mm});
            skLineSegment(sketch, "E83", {"start": v(-14.98, 108) * mm, "end": v(-32.98, 90) * mm});
            skLineSegment(sketch, "E84", {"start": v(15.68, 108) * mm, "end": v(33.68, 90) * mm});
            skPoint(sketch, "E85.endSnap0", {"position": v(80, 0) * mm});
            skLineSegment(sketch, "E86", {"start": v(0, 0) * mm, "end": v(-126.78, 0) * mm, "construction": true});
            skPoint(sketch, "E86.endSnap0", {"position": v(-60, 0) * mm});
            skLineSegment(sketch, "E87.MirrorCS", {"start": v(-14.98, -120.85) * mm, "end": v(-14.98, -108) * mm});
            skLineSegment(sketch, "E88.MirrorCS", {"start": v(14.98, -120.83) * mm, "end": v(15.68, -108) * mm});
            skLineSegment(sketch, "E89.MirrorCS", {"start": v(-14.98, -108) * mm, "end": v(-32.98, -90) * mm});
            skLineSegment(sketch, "E90.MirrorCS", {"start": v(15.68, -108) * mm, "end": v(33.68, -90) * mm});
            skCircle(sketch, "E91.MirrorC", {"center": v(0, -120) * mm, "radius": 6 * mm});
            skArc(sketch, "E92.MirrorCS", {"start": v(14.98, -120.83) * mm, "mid": v(0, -135) * mm, "end": v(-14.98, -120.85) * mm});
            skSolve(sketch);
        }
        {
            var Q0;
            Q0=makeQuery(id+"F16.imprint","IMPRINT",FACE,{"disambiguationData":[TD([[makeQuery(id+"F16.imprint","IMPRINT",EDGE,{"derivedFrom":sQuery(id+"F16.wireOp",EDGE,"E79")}),-1.0]])]});
            var Q1;
            Q1=makeQuery(id+"F16.imprint","IMPRINT",FACE,{"disambiguationData":[TD([[makeQuery(id+"F16.imprint","IMPRINT",EDGE,{"derivedFrom":sQuery(id+"F16.wireOp",EDGE,"E87.MirrorCS")}),-1.0]])]});
            var Q2;
            Q2=makeQuery(id+"F16.imprint","IMPRINT",FACE,{"disambiguationData":[TD([[makeQuery(id+"F16.imprint","IMPRINT",EDGE,{"derivedFrom":makeQuery(id+"F1.opExtrude","CAP_EDGE",EDGE,{"disambiguationData":[OSD([sQuery(id+"F0.wireOp",EDGE,"E1.left")])],"isStart":true})}),-1.0]])]});
            var Q3;
            Q3=makeQuery(id+"F2.opExtrude","CAP_FACE",FACE,{"disambiguationData":[OSD([sQuery(id+"F0.wireOp",EDGE,"E12"),sQuery(id+"F0.wireOp",EDGE,"E13"),sQuery(id+"F0.wireOp",EDGE,"E14"),sQuery(id+"F0.wireOp",EDGE,"E15"),sQuery(id+"F0.wireOp",EDGE,"E17.filletArc"),sQuery(id+"F0.wireOp",EDGE,"E18.filletArc"),sQuery(id+"F0.wireOp",EDGE,"E19.filletArc"),sQuery(id+"F0.wireOp",EDGE,"E20.filletArc"),sQuery(id+"F0.wireOp",EDGE,"E25.0"),sQuery(id+"F0.wireOp",EDGE,"E25.1"),sQuery(id+"F0.wireOp",EDGE,"E25.2"),sQuery(id+"F0.wireOp",EDGE,"E25.3"),sQuery(id+"F0.wireOp",EDGE,"E25.4"),sQuery(id+"F0.wireOp",EDGE,"E25.5"),sQuery(id+"F0.wireOp",EDGE,"E25.6"),sQuery(id+"F0.wireOp",EDGE,"E25.7")])],"isStart":false});
            extrude(context, id + "F17", {"entities" : qUnion([Q0, Q1, Q2]), "endBound" : BoundingType.UP_TO_SURFACE, "endBoundEntityFace" : qUnion([Q3]), "depth" : 25 * mm});
        }
    });
